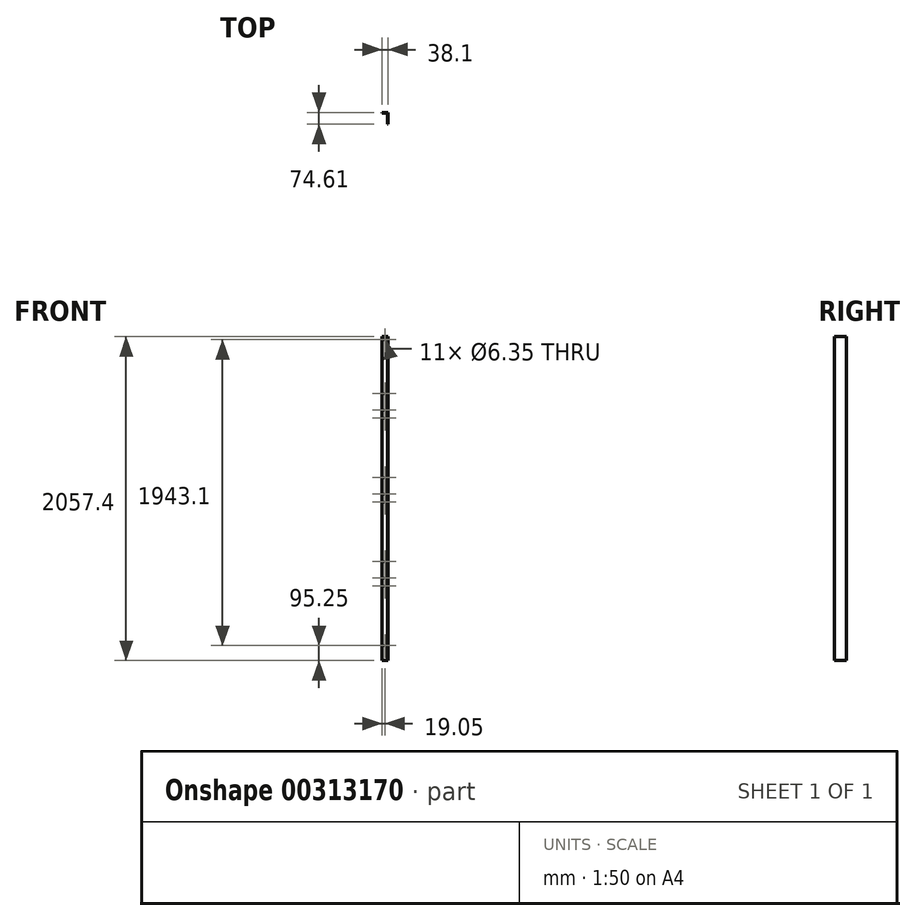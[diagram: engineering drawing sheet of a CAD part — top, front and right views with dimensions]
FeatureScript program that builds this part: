
annotation { "Feature Type Name" : "Feature", "Feature Type Description" : "" }
export const myFeature = defineFeature(function(context is Context, id is Id, definition is map)
    precondition{}
    {
        {
            var Q0;
            Q0=qCreatedBy(makeId("Top.planeOp"),FACE);
            var sketch = newSketch(context, id + "F0", { "sketchPlane" : qUnion([Q0])});
            skLineSegment(sketch, "E0.bottom", {"start": v(0, 0) * mm, "end": v(38.1, 0) * mm});
            skLineSegment(sketch, "E0.top", {"start": v(0, 74.61) * mm, "end": v(38.1, 74.61) * mm});
            skLineSegment(sketch, "E0.left", {"start": v(0, 0) * mm, "end": v(0, 74.61) * mm});
            skLineSegment(sketch, "E0.right", {"start": v(38.1, 0) * mm, "end": v(38.1, 74.61) * mm});
            skSolve(sketch);
        }
        {
            var Q0;
            Q0=qSketchRegion(id+"F0",true);
            extrude(context, id + "F1", {"entities" : qUnion([Q0]), "endBound" : BoundingType.SYMMETRIC, "depth" : 2057.4 * mm});
        }
        {
            var Q0;
            Q0=makeQuery(id+"F1.opExtrude","CAP_FACE",FACE,{"disambiguationData":[OSD([sQuery(id+"F0.wireOp",EDGE,"E0.bottom"),sQuery(id+"F0.wireOp",EDGE,"E0.top"),sQuery(id+"F0.wireOp",EDGE,"E0.left"),sQuery(id+"F0.wireOp",EDGE,"E0.right")])],"isStart":false});
            var Q1;
            Q1=makeQuery(id+"F1.opExtrude","SWEPT_FACE",FACE,{"disambiguationData":[OSD([sQuery(id+"F0.wireOp",EDGE,"E0.bottom")])]});
            var Q2;
            Q2=makeQuery(id+"F1.opExtrude","CAP_FACE",FACE,{"disambiguationData":[OSD([sQuery(id+"F0.wireOp",EDGE,"E0.bottom"),sQuery(id+"F0.wireOp",EDGE,"E0.top"),sQuery(id+"F0.wireOp",EDGE,"E0.left"),sQuery(id+"F0.wireOp",EDGE,"E0.right")])],"isStart":true});
            var Q3;
            Q3=makeQuery(id+"F1.opExtrude","SWEPT_FACE",FACE,{"disambiguationData":[OSD([sQuery(id+"F0.wireOp",EDGE,"E0.left")])]});
            shell(context, id + "F2", {"entities" : qUnion([Q0, Q1, Q2, Q3]), "thickness" : 2.78 * mm});
        }
        {
            var Q0;
            Q0=makeQuery(id+"F1.opExtrude","SWEPT_FACE",FACE,{"disambiguationData":[OSD([sQuery(id+"F0.wireOp",EDGE,"E0.top")])]});
            var sketch = newSketch(context, id + "F3", { "sketchPlane" : qUnion([Q0])});
            skCircle(sketch, "E1", {"center": v(-19.05, 561.98) * mm, "radius": 3.18 * mm});
            skCircle(sketch, "E2", {"center": v(-19.05, 511.18) * mm, "radius": 3.18 * mm});
            skCircle(sketch, "E3", {"center": v(-19.05, 133.35) * mm, "radius": 3.18 * mm});
            skCircle(sketch, "E4.0.1.0", {"center": v(-19.05, -22.23) * mm, "radius": 3.18 * mm});
            skCircle(sketch, "E4.0.1.1", {"center": v(-19.05, 28.57) * mm, "radius": 3.18 * mm});
            skCircle(sketch, "E4.0.1.2", {"center": v(-19.05, -400.05) * mm, "radius": 3.18 * mm});
            skCircle(sketch, "E4.0.2.0", {"center": v(-19.05, -555.63) * mm, "radius": 3.18 * mm});
            skCircle(sketch, "E4.0.2.1", {"center": v(-19.05, -504.83) * mm, "radius": 3.18 * mm});
            skCircle(sketch, "E4.0.2.2", {"center": v(-19.05, -933.45) * mm, "radius": 3.18 * mm});
            skLineSegment(sketch, "E4.direction1", {"start": v(-19.05, 133.35) * mm, "end": v(0, 133.35) * mm, "construction": true});
            skLineSegment(sketch, "E4.direction2", {"start": v(-19.05, 133.35) * mm, "end": v(-19.05, -400.05) * mm, "construction": true});
            skCircle(sketch, "E5", {"center": v(-19.05, 666.75) * mm, "radius": 3.18 * mm});
            skCircle(sketch, "E6", {"center": v(-19.05, 1009.65) * mm, "radius": 3.18 * mm});
            skSolve(sketch);
        }
        {
            var Q0;
            Q0=qSketchRegion(id+"F3",true);
            extrude(context, id + "F4", {"entities" : qUnion([Q0]), "operationType" : NewBodyOperationType.REMOVE, "endBound" : BoundingType.THROUGH_ALL, "oppositeDirection" : true, "depth" : 25.4 * mm});
        }
    });
